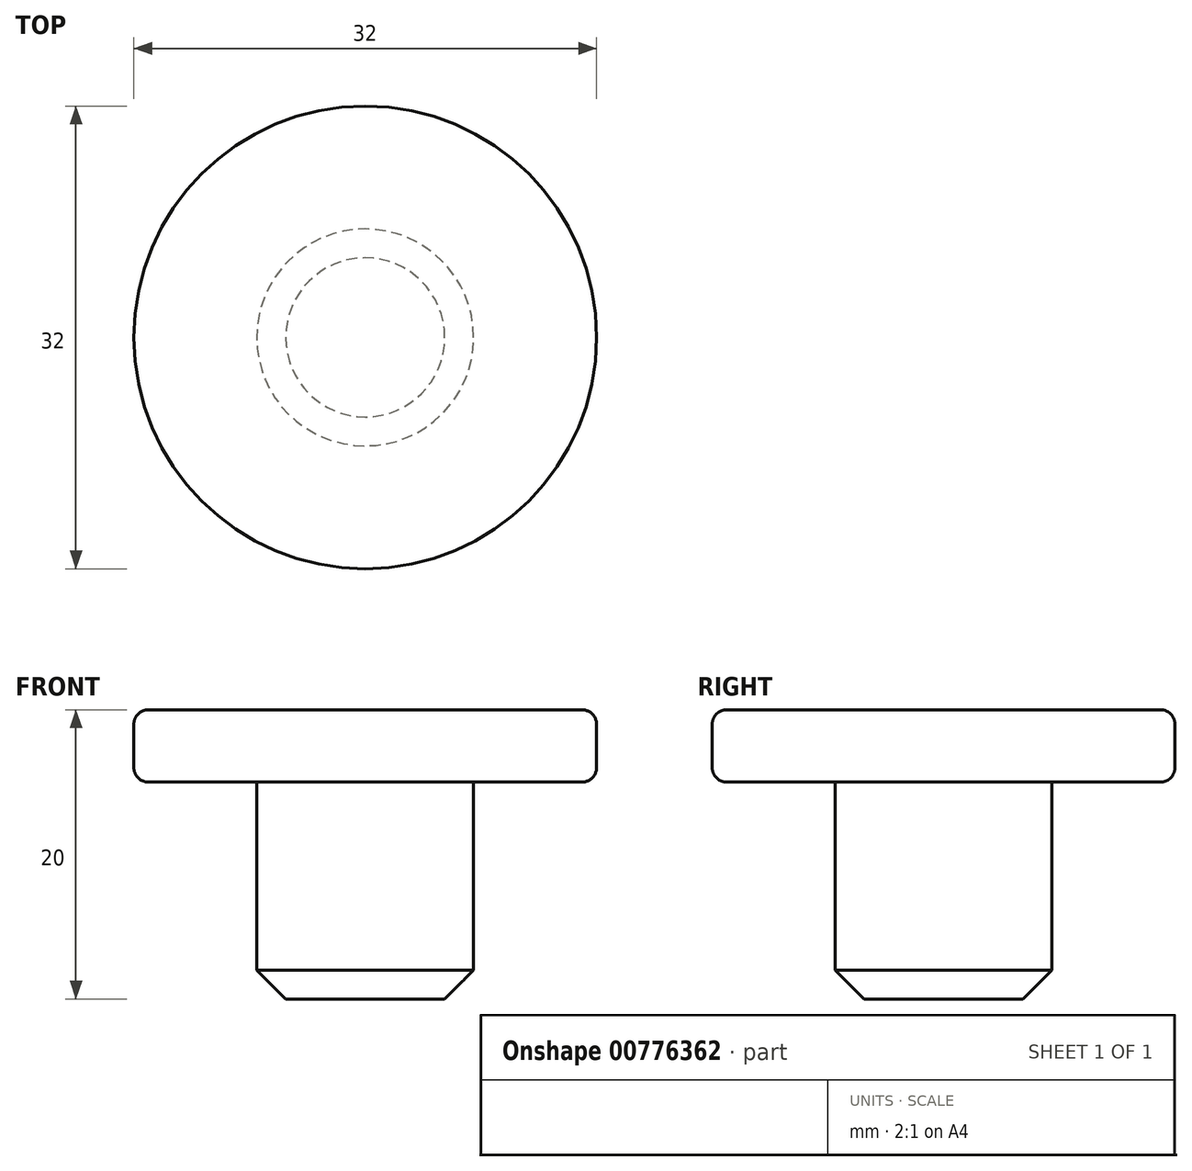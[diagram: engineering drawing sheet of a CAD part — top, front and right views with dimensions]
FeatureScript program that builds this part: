
annotation { "Feature Type Name" : "Feature", "Feature Type Description" : "" }
export const myFeature = defineFeature(function(context is Context, id is Id, definition is map)
    precondition{}
    {
        {
            var Q0;
            Q0=qCreatedBy(makeId("Top.planeOp"),FACE);
            var sketch = newSketch(context, id + "F0", { "sketchPlane" : qUnion([Q0])});
            skCircle(sketch, "E0", {"center": v(0, 0) * mm, "radius": 7.5 * mm});
            skSolve(sketch);
        }
        {
            var Q0;
            Q0=makeQuery(id+"F0.imprint","IMPRINT",FACE,{"disambiguationData":[TD([[makeQuery(id+"F0.imprint","IMPRINT",EDGE,{"derivedFrom":sQuery(id+"F0.wireOp",EDGE,"E0")}),1.0]])]});
            extrude(context, id + "F1", {"entities" : qUnion([Q0]), "depth" : 15 * mm, "offsetDistance" : 25 * mm});
        }
        {
            var Q0;
            Q0=makeQuery(id+"F1.opExtrude","CAP_FACE",FACE,{"disambiguationData":[OSD([sQuery(id+"F0.wireOp",EDGE,"E0")])],"isStart":false});
            var sketch = newSketch(context, id + "F2", { "sketchPlane" : qUnion([Q0])});
            skCircle(sketch, "E1", {"center": v(0, 0) * mm, "radius": 16 * mm});
            skSolve(sketch);
        }
        {
            var Q0;
            Q0 = qSketchRegion(id + "F2", true);
            extrude(context, id + "F3", {"entities" : qUnion([Q0]), "operationType" : NewBodyOperationType.ADD, "depth" : 5 * mm, "offsetDistance" : 25 * mm});
        }
        {
            var Q0;
            Q0=makeQuery(id+"F3.opExtrude","CAP_EDGE",EDGE,{"disambiguationData":[OSD([sQuery(id+"F2.wireOp",EDGE,"E1")])],"isStart":false});
            var Q1;
            Q1=makeQuery(id+"F3.opExtrude","CAP_EDGE",EDGE,{"disambiguationData":[OSD([sQuery(id+"F2.wireOp",EDGE,"E1")])],"isStart":true});
            fillet(context, id + "F4", {"entities" : qUnion([Q0, Q1]), "radius" : 1 * mm, "tangentPropagation" : true, "allowEdgeOverflow" : false});
        }
        {
            var Q0;
            Q0=makeQuery(id+"F1.opExtrude","CAP_EDGE",EDGE,{"disambiguationData":[OSD([sQuery(id+"F0.wireOp",EDGE,"E0")])],"isStart":true});
            chamfer(context, id + "F5", {"entities" : qUnion([Q0]), "width" : 2 * mm, "tangentPropagation" : true});
        }
    });
